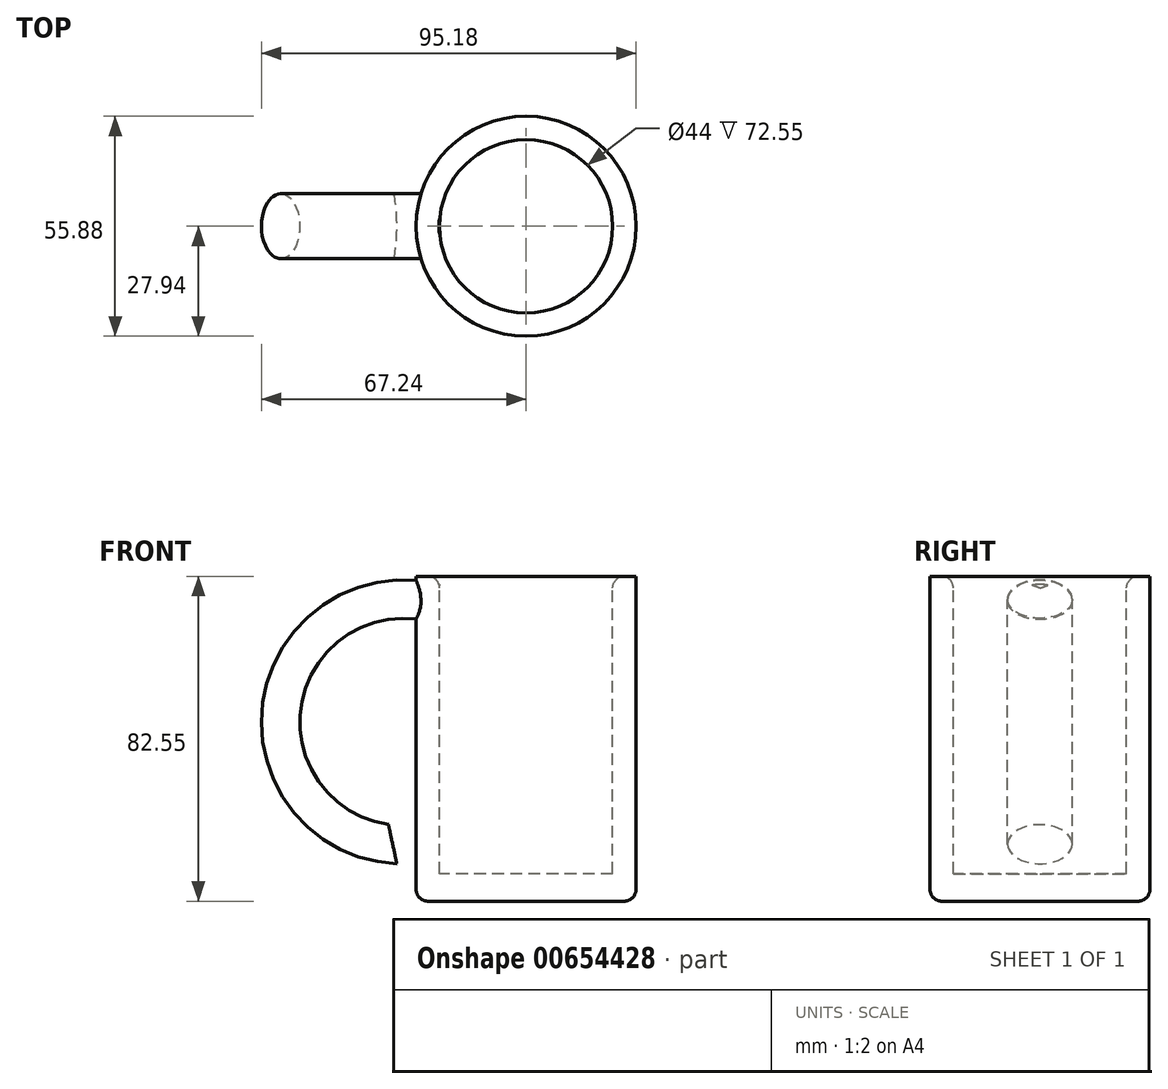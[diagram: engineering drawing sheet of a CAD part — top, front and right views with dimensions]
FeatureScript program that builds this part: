
annotation { "Feature Type Name" : "Feature", "Feature Type Description" : "" }
export const myFeature = defineFeature(function(context is Context, id is Id, definition is map)
    precondition{}
    {
        {
            var Q0;
            Q0=qCreatedBy(makeId("Front.planeOp"),FACE);
            var sketch = newSketch(context, id + "F0", { "sketchPlane" : qUnion([Q0])});
            skLineSegment(sketch, "E0", {"start": v(0, 0) * mm, "end": v(-27.94, 0) * mm});
            skLineSegment(sketch, "E1", {"start": v(-27.94, 0) * mm, "end": v(-27.94, 82.55) * mm});
            skLineSegment(sketch, "E2", {"start": v(-27.94, 82.55) * mm, "end": v(-22, 82.55) * mm});
            skLineSegment(sketch, "E3", {"start": v(-22, 82.55) * mm, "end": v(-22, 7) * mm});
            skLineSegment(sketch, "E4", {"start": v(-22, 7) * mm, "end": v(0, 7) * mm});
            skLineSegment(sketch, "E5", {"start": v(0, 7) * mm, "end": v(0, 0) * mm});
            skSolve(sketch);
        }
        {
            var Q0;
            Q0 = qSketchRegion(id + "F0", true);
            var Q1;
            Q1=sQuery(id+"F0.wireOp",EDGE,"E5");
            revolve(context, id + "F1", {"entities" : qUnion([Q0]), "axis" : qUnion([Q1]), "revolveType" : RevolveType.FULL, "surfaceOperationType" : NewSurfaceOperationType.NEW});
        }
        {
            var Q0;
            Q0=makeQuery(id+"F1.opRevolve","SWEPT_EDGE",EDGE,{"disambiguationData":[OSD([sQuery(id+"F0.wireOp",EDGE,"E2"),sQuery(id+"F0.wireOp",EDGE,"E3")])]});
            var Q1;
            Q1=makeQuery(id+"F1.opRevolve","SWEPT_EDGE",EDGE,{"disambiguationData":[OSD([sQuery(id+"F0.wireOp",EDGE,"E0"),sQuery(id+"F0.wireOp",EDGE,"E1")])]});
            fillet(context, id + "F2", {"entities" : qUnion([Q0, Q1]), "radius" : 3 * mm, "tangentPropagation" : true, "allowEdgeOverflow" : false});
        }
        {
            var Q0;
            Q0=sQuery(id+"F0.wireOp",EDGE,"E3");
            cPlane(context, id + "F3", {"entities" : qUnion([Q0]), "cplaneType" : CPlaneType.LINE_ANGLE, "offset" : 25.4 * mm, "angle" : 0 * degree, "width" : 152.4 * mm, "height" : 152.4 * mm});
        }
        {
            var Q0;
            Q0=qCreatedBy(makeId("Front.planeOp"),FACE);
            var sketch = newSketch(context, id + "F4", { "sketchPlane" : qUnion([Q0])});
            skArc(sketch, "E6", {"start": v(-27.96, 75.1) * mm, "mid": v(-60.88, 45.62) * mm, "end": v(-28.12, 15.96) * mm});
            skSolve(sketch);
        }
        {
            var Q0;
            Q0=qCreatedBy(id+"F3.planeOp",FACE);
            var sketch = newSketch(context, id + "F5", { "sketchPlane" : qUnion([Q0])});
            skEllipse(sketch, "E7", {"center": v(0, 75.34) * mm, "majorRadius": 8.24 * mm, "minorRadius": 5.1 * mm, "majorAxis": v(1, 0)});
            skSolve(sketch);
        }
        {
            var Q0;
            Q0=makeQuery(id+"F5.imprint","IMPRINT",FACE,{"disambiguationData":[TD([[makeQuery(id+"F5.imprint","IMPRINT",EDGE,{"derivedFrom":sQuery(id+"F5.wireOp",EDGE,"E7")}),1.0]])]});
            var Q1;
            Q1=sQuery(id+"F4.wireOp",EDGE,"E6");
            sweep(context, id + "F6", {"operationType" : NewBodyOperationType.ADD, "profiles" : qUnion([Q0]), "path" : qUnion([Q1])});
        }
    });
